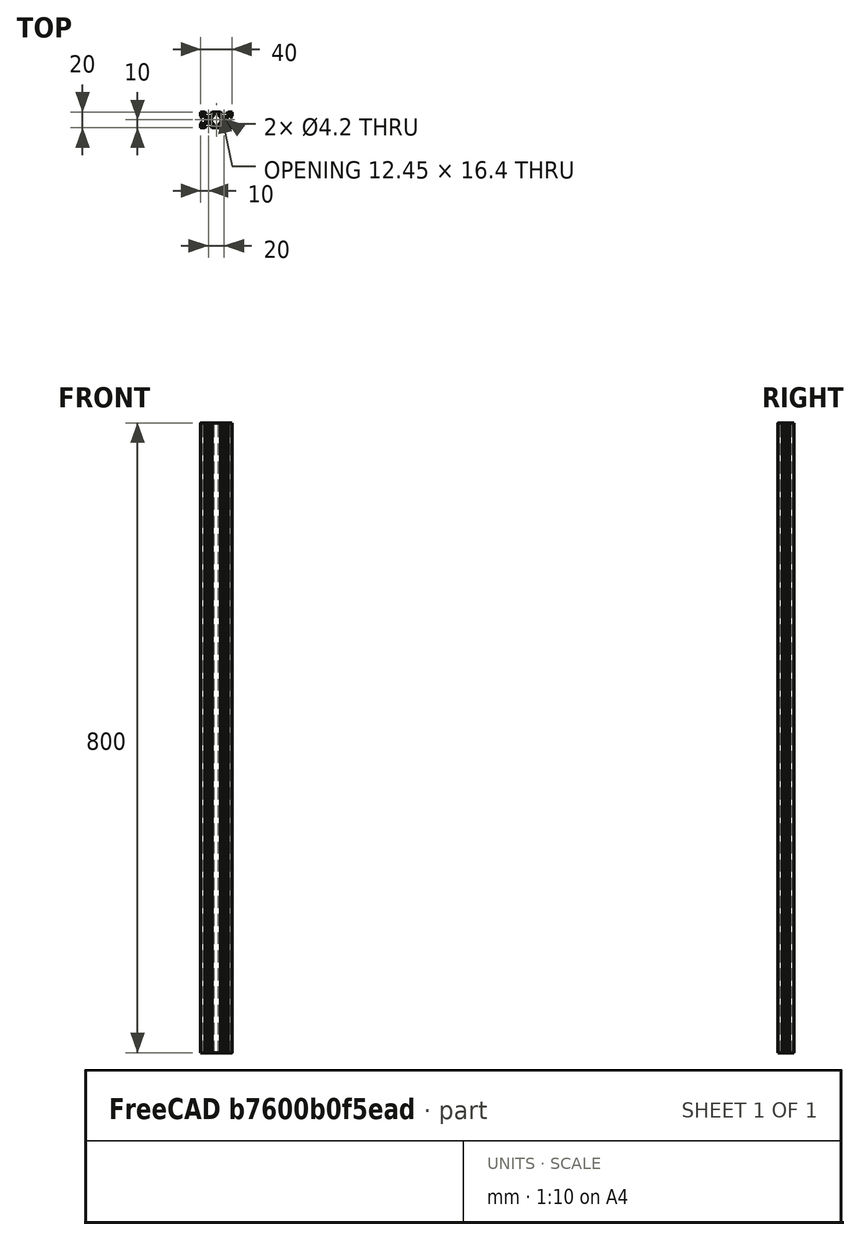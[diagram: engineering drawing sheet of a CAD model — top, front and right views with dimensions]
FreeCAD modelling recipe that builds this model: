
FCSTD DOCUMENT  (FreeCAD 0.20R25566 (Git))
Label: 2040-800
License: All rights reserved
LicenseURL: http://en.wikipedia.org/wiki/All_rights_reserved
objects: Sketcher::SketchObject×1, PartDesign::Pad×1, PartDesign::Body×1
note: 4 computed .brp shape members not serialized (recipe doc carries the construction recipe); baked Part::Feature solids carry a one-line shape summary decoded from their .brp

FEATURE [Sketcher::SketchObject] Sketch
  FullyConstrained = true
  MapMode = 5
  Support = -> [XY_Plane]
  sketch-geometry (114):
    g0: LineSegment StartX=-10 StartY=4.58 StartZ=0 EndX=-10 EndY=9.5 EndZ=0
    g1: LineSegment StartX=-9.5 StartY=10 StartZ=0 EndX=-4.58 EndY=10 EndZ=0
    g2: LineSegment StartX=-5.5 StartY=8.2 StartZ=0 EndX=-3.125 EndY=8.2 EndZ=0
    g3: LineSegment StartX=-8.2 StartY=5.5 StartZ=0 EndX=-8.2 EndY=3.125 EndZ=0
    g4: LineSegment StartX=-0.125 StartY=3.9 StartZ=0 EndX=-2.83934 EndY=3.9 EndZ=0
    g5: LineSegment StartX=-3.9 StartY=2.83934 StartZ=0 EndX=-3.9 EndY=0.125 EndZ=0
    g6: ArcOfCircle CenterX=0 CenterY=3.9 CenterZ=0 NormalX=0 NormalY=0 NormalZ=1 AngleXU=0 Radius=0.125 StartAngle=3.14159 EndAngle=6.28319
    g7: ArcOfCircle CenterX=-3.9 CenterY=0 CenterZ=0 NormalX=0 NormalY=0 NormalZ=1 AngleXU=0 Radius=0.125 StartAngle=4.71239 EndAngle=7.85398
    g8: ArcOfCircle CenterX=-9.5 CenterY=9.5 CenterZ=0 NormalX=0 NormalY=0 NormalZ=1 AngleXU=0 Radius=0.5 StartAngle=1.5708 EndAngle=3.14159
    g9: LineSegment StartX=-5.5 StartY=8.2 StartZ=0 EndX=-5.5 EndY=6.56066 EndZ=0
    g10: LineSegment StartX=-8.2 StartY=5.5 StartZ=0 EndX=-6.56066 EndY=5.5 EndZ=0
    g11: LineSegment StartX=-4.58 StartY=10 StartZ=0 EndX=-3.125 EndY=8.545 EndZ=0
    g12: LineSegment StartX=-3.125 StartY=8.545 StartZ=0 EndX=-3.125 EndY=8.2 EndZ=0
    g13: LineSegment StartX=-10 StartY=4.58 StartZ=0 EndX=-8.545 EndY=3.125 EndZ=0
    g14: LineSegment StartX=-8.545 StartY=3.125 StartZ=0 EndX=-8.2 EndY=3.125 EndZ=0
    g15: LineSegment StartX=-5.5 StartY=6.56066 StartZ=0 EndX=-2.83934 EndY=3.9 EndZ=0
    g16: LineSegment StartX=-6.56066 StartY=5.5 StartZ=0 EndX=-3.9 EndY=2.83934 EndZ=0
    g17: Circle CenterX=0 CenterY=0 CenterZ=0 NormalX=0 NormalY=0 NormalZ=1 AngleXU=0 Radius=2.1
    g18: LineSegment StartX=0.125 StartY=3.9 StartZ=0 EndX=2.83934 EndY=3.9 EndZ=0
    g19: LineSegment StartX=2.83934 StartY=3.9 StartZ=0 EndX=5.5 EndY=6.56066 EndZ=0
    g20: LineSegment StartX=5.5 StartY=6.56066 StartZ=0 EndX=5.5 EndY=8.2 EndZ=0
    g21: LineSegment StartX=3.125 StartY=8.2 StartZ=0 EndX=3.125 EndY=8.545 EndZ=0
    g22: LineSegment StartX=5.5 StartY=8.2 StartZ=0 EndX=3.125 EndY=8.2 EndZ=0
    g23: LineSegment StartX=7 StartY=5.93934 StartZ=0 EndX=3.9 EndY=2.83934 EndZ=0
    g24: LineSegment StartX=3.9 StartY=2.83934 StartZ=0 EndX=3.9 EndY=0.125 EndZ=0
    g25: ArcOfCircle CenterX=3.9 CenterY=0 CenterZ=0 NormalX=0 NormalY=0 NormalZ=1 AngleXU=0 Radius=0.125 StartAngle=1.5708 EndAngle=4.71239
    g26: LineSegment StartX=3.9 StartY=-0.125 StartZ=0 EndX=3.9 EndY=-2.83934 EndZ=0
    g27: LineSegment StartX=3.9 StartY=-2.83934 StartZ=0 EndX=7 EndY=-5.93934 EndZ=0
    g28: LineSegment StartX=4.58 StartY=-10 StartZ=0 EndX=3.125 EndY=-8.545 EndZ=0
    g29: LineSegment StartX=2.83934 StartY=-3.9 StartZ=0 EndX=5.5 EndY=-6.56066 EndZ=0
    g30: LineSegment StartX=3.125 StartY=-8.545 StartZ=0 EndX=3.125 EndY=-8.2 EndZ=0
    g31: LineSegment StartX=3.125 StartY=-8.2 StartZ=0 EndX=5.5 EndY=-8.2 EndZ=0
    g32: LineSegment StartX=5.5 StartY=-8.2 StartZ=0 EndX=5.5 EndY=-6.56066 EndZ=0
    g33: ArcOfCircle CenterX=0 CenterY=-3.9 CenterZ=0 NormalX=0 NormalY=0 NormalZ=1 AngleXU=0 Radius=0.125 StartAngle=0 EndAngle=3.14159
    g34: LineSegment StartX=0.125 StartY=-3.9 StartZ=0 EndX=2.83934 EndY=-3.9 EndZ=0
    g35: LineSegment StartX=-0.125 StartY=-3.9 StartZ=0 EndX=-2.83934 EndY=-3.9 EndZ=0
    g36: LineSegment StartX=-3.9 StartY=-0.125 StartZ=0 EndX=-3.9 EndY=-2.83934 EndZ=0
    g37: LineSegment StartX=-3.9 StartY=-2.83934 StartZ=0 EndX=-6.56066 EndY=-5.5 EndZ=0
    g38: LineSegment StartX=-6.56066 StartY=-5.5 StartZ=0 EndX=-8.2 EndY=-5.5 EndZ=0
    g39: LineSegment StartX=-8.2 StartY=-5.5 StartZ=0 EndX=-8.2 EndY=-3.125 EndZ=0
    g40: LineSegment StartX=-8.2 StartY=-3.125 StartZ=0 EndX=-8.545 EndY=-3.125 EndZ=0
    g41: LineSegment StartX=-8.545 StartY=-3.125 StartZ=0 EndX=-10 EndY=-4.58 EndZ=0
    g42: LineSegment StartX=-10 StartY=-4.58 StartZ=0 EndX=-10 EndY=-9.5 EndZ=0
    g43: ArcOfCircle CenterX=-9.5 CenterY=-9.5 CenterZ=0 NormalX=0 NormalY=0 NormalZ=1 AngleXU=0 Radius=0.5 StartAngle=3.14159 EndAngle=4.71239
    g44: LineSegment StartX=-9.5 StartY=-10 StartZ=0 EndX=-4.58 EndY=-10 EndZ=0
    g45: LineSegment StartX=-4.58 StartY=-10 StartZ=0 EndX=-3.125 EndY=-8.545 EndZ=0
    g46: LineSegment StartX=-2.83934 StartY=-3.9 StartZ=0 EndX=-5.5 EndY=-6.56066 EndZ=0
    g47: LineSegment StartX=-5.5 StartY=-6.56066 StartZ=0 EndX=-5.5 EndY=-8.2 EndZ=0
    g48: LineSegment StartX=-5.5 StartY=-8.2 StartZ=0 EndX=-3.125 EndY=-8.2 EndZ=0
    g49: LineSegment StartX=-3.125 StartY=-8.545 StartZ=0 EndX=-3.125 EndY=-8.2 EndZ=0
    g50: LineSegment StartX=3.125 StartY=8.545 StartZ=0 EndX=4.58 EndY=10 EndZ=0
    g51: LineSegment StartX=-3.9 StartY=2.83934 StartZ=0 EndX=-2.83934 EndY=3.9 EndZ=0
    g52: LineSegment StartX=3.9 StartY=2.83934 StartZ=0 EndX=2.83934 EndY=3.9 EndZ=0
    g53: LineSegment StartX=4.58 StartY=10 StartZ=0 EndX=15.42 EndY=10 EndZ=0
    g54: LineSegment StartX=4.58 StartY=-10 StartZ=0 EndX=15.42 EndY=-10 EndZ=0
    g55: LineSegment StartX=7 StartY=5.93934 StartZ=0 EndX=7 EndY=8.2 EndZ=0
    g56: LineSegment StartX=5.5 StartY=8.2 StartZ=0 EndX=7 EndY=8.2 EndZ=0
    g57: LineSegment StartX=7 StartY=-5.93934 StartZ=0 EndX=7 EndY=-8.2 EndZ=0
    g58: LineSegment StartX=7 StartY=8.2 StartZ=0 EndX=13 EndY=8.2 EndZ=0
    g59: LineSegment StartX=15.42 StartY=10 StartZ=0 EndX=16.875 EndY=8.545 EndZ=0
    g60: LineSegment StartX=16.875 StartY=8.545 StartZ=0 EndX=16.875 EndY=8.2 EndZ=0
    g61: LineSegment StartX=16.875 StartY=8.2 StartZ=0 EndX=14.5 EndY=8.2 EndZ=0
    g62: LineSegment StartX=15.42 StartY=-10 StartZ=0 EndX=16.875 EndY=-8.545 EndZ=0
    g63: LineSegment StartX=16.875 StartY=-8.545 StartZ=0 EndX=16.875 EndY=-8.2 EndZ=0
    g64: LineSegment StartX=16.875 StartY=-8.2 StartZ=0 EndX=14.5 EndY=-8.2 EndZ=0
    g65: LineSegment StartX=7 StartY=-8.2 StartZ=0 EndX=13 EndY=-8.2 EndZ=0
    g66: LineSegment StartX=13 StartY=8.2 StartZ=0 EndX=14.5 EndY=8.2 EndZ=0
    g67: LineSegment StartX=13 StartY=8.2 StartZ=0 EndX=13 EndY=5.93934 EndZ=0
    g68: LineSegment StartX=13 StartY=-8.2 StartZ=0 EndX=13 EndY=-5.93934 EndZ=0
    g69: LineSegment StartX=14.5 StartY=8.2 StartZ=0 EndX=14.5 EndY=6.56066 EndZ=0
    g70: LineSegment StartX=14.5 StartY=-8.2 StartZ=0 EndX=14.5 EndY=-6.56066 EndZ=0
    g71: LineSegment StartX=13 StartY=5.93934 StartZ=0 EndX=16.1 EndY=2.83934 EndZ=0
    g72: LineSegment StartX=14.5 StartY=6.56066 StartZ=0 EndX=17.1607 EndY=3.9 EndZ=0
    g73: LineSegment StartX=13 StartY=-5.93934 StartZ=0 EndX=16.1 EndY=-2.83934 EndZ=0
    g74: LineSegment StartX=14.5 StartY=-6.56066 StartZ=0 EndX=17.1607 EndY=-3.9 EndZ=0
    g75: LineSegment StartX=16.1 StartY=2.83934 StartZ=0 EndX=16.1 EndY=0.125 EndZ=0
    g76: LineSegment StartX=16.1 StartY=-2.83934 StartZ=0 EndX=16.1 EndY=-0.125 EndZ=0
    g77: ArcOfCircle CenterX=16.1 CenterY=0 CenterZ=0 NormalX=0 NormalY=0 NormalZ=1 AngleXU=0 Radius=0.125 StartAngle=4.71239 EndAngle=7.85398
    g78: LineSegment StartX=17.1607 StartY=3.9 StartZ=0 EndX=19.875 EndY=3.9 EndZ=0
    g79: LineSegment StartX=17.1607 StartY=-3.9 StartZ=0 EndX=19.875 EndY=-3.9 EndZ=0
    g80: LineSegment StartX=20.125 StartY=3.9 StartZ=0 EndX=22.8393 EndY=3.9 EndZ=0
    g81: LineSegment StartX=20.125 StartY=-3.9 StartZ=0 EndX=22.8393 EndY=-3.9 EndZ=0
    g82: ArcOfCircle CenterX=20 CenterY=-3.9 CenterZ=0 NormalX=0 NormalY=0 NormalZ=1 AngleXU=0 Radius=0.125 StartAngle=-9e-16 EndAngle=3.14159
    g83: ArcOfCircle CenterX=20 CenterY=3.9 CenterZ=0 NormalX=0 NormalY=0 NormalZ=1 AngleXU=0 Radius=0.125 StartAngle=3.14159 EndAngle=6.28319
    g84: Circle CenterX=20 CenterY=0 CenterZ=0 NormalX=0 NormalY=0 NormalZ=1 AngleXU=0 Radius=2.1
    g85: LineSegment StartX=22.8393 StartY=3.9 StartZ=0 EndX=25.5 EndY=6.56066 EndZ=0
    g86: LineSegment StartX=22.8393 StartY=-3.9 StartZ=0 EndX=25.5 EndY=-6.56066 EndZ=0
    g87: LineSegment StartX=25.5 StartY=6.56066 StartZ=0 EndX=25.5 EndY=8.2 EndZ=0
    g88: LineSegment StartX=25.5 StartY=-6.56066 StartZ=0 EndX=25.5 EndY=-8.2 EndZ=0
    g89: LineSegment StartX=25.5 StartY=8.2 StartZ=0 EndX=23.125 EndY=8.2 EndZ=0
    g90: LineSegment StartX=25.5 StartY=-8.2 StartZ=0 EndX=23.125 EndY=-8.2 EndZ=0
    g91: LineSegment StartX=23.125 StartY=8.2 StartZ=0 EndX=23.125 EndY=8.545 EndZ=0
    g92: LineSegment StartX=23.125 StartY=-8.2 StartZ=0 EndX=23.125 EndY=-8.545 EndZ=0
    g93: LineSegment StartX=23.125 StartY=8.545 StartZ=0 EndX=24.58 EndY=10 EndZ=0
    g94: LineSegment StartX=23.125 StartY=-8.545 StartZ=0 EndX=24.58 EndY=-10 EndZ=0
    g95: LineSegment StartX=24.58 StartY=10 StartZ=0 EndX=29.5 EndY=10 EndZ=0
    g96: LineSegment StartX=24.58 StartY=-10 StartZ=0 EndX=29.5 EndY=-10 EndZ=0
    g97: ArcOfCircle CenterX=29.5 CenterY=9.5 CenterZ=0 NormalX=0 NormalY=0 NormalZ=1 AngleXU=0 Radius=0.5 StartAngle=9e-16 EndAngle=1.5708
    g98: ArcOfCircle CenterX=29.5 CenterY=-9.5 CenterZ=0 NormalX=0 NormalY=0 NormalZ=1 AngleXU=0 Radius=0.5 StartAngle=4.71239 EndAngle=6.28319
    g99: LineSegment StartX=30 StartY=9.5 StartZ=0 EndX=30 EndY=4.58 EndZ=0
    g100: LineSegment StartX=30 StartY=-9.5 StartZ=0 EndX=30 EndY=-4.58 EndZ=0
    g101: LineSegment StartX=30 StartY=-4.58 StartZ=0 EndX=28.545 EndY=-3.125 EndZ=0
    g102: LineSegment StartX=30 StartY=4.58 StartZ=0 EndX=28.545 EndY=3.125 EndZ=0
    g103: LineSegment StartX=28.545 StartY=3.125 StartZ=0 EndX=28.2 EndY=3.125 EndZ=0
    g104: LineSegment StartX=28.545 StartY=-3.125 StartZ=0 EndX=28.2 EndY=-3.125 EndZ=0
    g105: LineSegment StartX=28.2 StartY=3.125 StartZ=0 EndX=28.2 EndY=5.5 EndZ=0
    g106: LineSegment StartX=28.2 StartY=-3.125 StartZ=0 EndX=28.2 EndY=-5.5 EndZ=0
    g107: LineSegment StartX=28.2 StartY=5.5 StartZ=0 EndX=26.5607 EndY=5.5 EndZ=0
    g108: LineSegment StartX=28.2 StartY=-5.5 StartZ=0 EndX=26.5607 EndY=-5.5 EndZ=0
    g109: LineSegment StartX=26.5607 StartY=5.5 StartZ=0 EndX=23.9 EndY=2.83934 EndZ=0
    g110: LineSegment StartX=26.5607 StartY=-5.5 StartZ=0 EndX=23.9 EndY=-2.83934 EndZ=0
    g111: LineSegment StartX=23.9 StartY=2.83934 StartZ=0 EndX=23.9 EndY=0.125 EndZ=0
    g112: LineSegment StartX=23.9 StartY=-2.83934 StartZ=0 EndX=23.9 EndY=-0.125 EndZ=0
    g113: ArcOfCircle CenterX=23.9 CenterY=3.14e-14 CenterZ=0 NormalX=0 NormalY=0 NormalZ=1 AngleXU=0 Radius=0.125 StartAngle=1.5708 EndAngle=4.71236
  constraints (345):
    c: Diameter(g17) = 4.2
    c: Radius(g25) = 0.125
    c: Coincident(g-1,g17)
    c: DistanceY(g43,g1) = 20
    c: Radius(g43) = 0.5
    c: DistanceX(g42,g17) = 10
    c: DistanceY(g43,g17) = 10
    c: Distance(g5,g4) = 1.5
    c: DistanceY(g18,g20) = 4.3
    c: DistanceX(g11,g21) = 6.25
    c: DistanceX(g1,g50) = 9.16
    c: DistanceX(g2,g20) = 11
    c: Coincident(g6,g18)
    c: Coincident(g6,g4)
    c: Coincident(g4,g15)
    c: Coincident(g18,g19)
    c: Coincident(g5,g16)
    c: Coincident(g16,g10)
    c: Coincident(g15,g9)
    c: Coincident(g12,g2)
    c: Coincident(g2,g9)
    c: Coincident(g12,g11)
    c: Coincident(g1,g11)
    c: Coincident(g22,g21)
    c: Coincident(g50,g21)
    c: Coincident(g22,g20)
    c: Coincident(g19,g20)
    c: Coincident(g0,g13)
    c: Coincident(g14,g13)
    c: Coincident(g14,g3)
    c: Coincident(g3,g10)
    c: Coincident(g5,g7)
    c: Coincident(g36,g7)
    c: Coincident(g37,g36)
    c: Coincident(g38,g37)
    c: Coincident(g38,g39)
    c: Coincident(g40,g39)
    c: Coincident(g41,g40)
    c: Coincident(g42,g41)
    c: Coincident(g44,g45)
    c: Coincident(g49,g45)
    c: Coincident(g48,g49)
    c: Coincident(g48,g47)
    c: Coincident(g46,g47)
    c: Coincident(g35,g46)
    c: Coincident(g33,g35)
    c: Coincident(g34,g33)
    c: Coincident(g34,g29)
    c: Coincident(g32,g29)
    c: Coincident(g31,g32)
    c: Coincident(g31,g30)
    c: Coincident(g28,g30)
    c: Coincident(g27,g26)
    c: Coincident(g24,g23)
    c: Coincident(g26,g25)
    c: Coincident(g25,g24)
    c: Vertical(g0)
    c: Horizontal(g1)
    c: Equal(g0,g1)
    c: Horizontal(g4)
    c: PointOnObject(g6,g-2)
    c: Horizontal(g18)
    c: Horizontal(g4,g6)
    c: Horizontal(g6,g6)
    c: Parallel(g13,g11)
    c: Horizontal(g14)
    c: Vertical(g12)
    c: Equal(g14,g12)
    c: Vertical(g3)
    c: Horizontal(g2)
    c: Equal(g3,g2)
    c: Equal(g10,g9)
    c: Horizontal(g10)
    c: Vertical(g9)
    c: Parallel(g16,g15)
    c: Equal(g13,g11)
    c: Tangent(g8,g0) = 1.5708
    c: PointOnObject(g7,g-1)
    c: Vertical(g5)
    c: Vertical(g36)
    c: Vertical(g7,g7)
    c: Vertical(g7,g5)
    c: Horizontal(g38)
    c: Vertical(g39)
    c: Horizontal(g40)
    c: Vertical(g42)
    c: Equal(g36,g5)
    c: Equal(g37,g16)
    c: Perpendicular(g16,g37)
    c: Equal(g38,g10)
    c: Equal(g39,g3)
    c: Equal(g40,g14)
    c: Equal(g41,g13)
    c: Perpendicular(g41,g13)
    c: Equal(g42,g0)
    c: Tangent(g43,g42) = -1.5708
    c: Tangent(g43,g44) = -1.5708
    c: Tangent(g8,g1) = 1.5708
    c: Equal(g43,g8)
    c: Horizontal(g44)
    c: Equal(g44,g42)
    c: Equal(g41,g45)
    c: Parallel(g41,g45)
    c: Vertical(g49)
    c: Equal(g49,g40)
    c: Horizontal(g48)
    c: Vertical(g47)
    c: Equal(g47,g38)
    c: Equal(g46,g37)
    c: Parallel(g46,g37)
    c: PointOnObject(g33,g-2)
    c: Horizontal(g33,g33)
    c: Horizontal(g33,g33)
    c: Horizontal(g35)
    c: Equal(g35,g36)
    c: Horizontal(g34)
    c: Vertical(g32)
    c: Perpendicular(g46,g29)
    c: Equal(g29,g46)
    c: Equal(g32,g47)
    c: Horizontal(g31)
    c: Equal(g31,g48)
    c: Vertical(g30)
    c: Equal(g30,g49)
    c: Perpendicular(g28,g45)
    c: Equal(g28,g45)
    c: Parallel(g29,g27)
    c: PointOnObject(g25,g-1)
    c: Vertical(g26)
    c: Vertical(g25,g24)
    c: Vertical(g24,g25)
    c: Equal(g34,g26)
    c: Equal(g33,g7)
    c: Equal(g7,g6)
    c: Vertical(g24)
    c: Equal(g26,g24)
    c: Equal(g4,g5)
    c: Equal(g4,g18)
    c: Parallel(g23,g19)
    c: Vertical(g20)
    c: Horizontal(g22)
    c: Equal(g22,g2)
    c: Vertical(g21)
    c: Equal(g11,g50)
    c: Horizontal(g2,g21)
    c: Vertical(g10,g37)
    c: Angle(g50,g11) = 1.5708
    c: DistanceY(g2,g1) = 1.8
    c: Equal(g21,g12)
    c: Horizontal(g36,g26)
    c: Vertical(g29,g18)
    c: Coincident(g51,g5)
    c: Coincident(g51,g4)
    c: Coincident(g52,g23)
    c: Coincident(g52,g18)
    c: Equal(g52,g51)
    c: Equal(g15,g19)
    c: Equal(g20,g9)
    c: Horizontal(g53)
    c: Horizontal(g54)
    c: Coincident(g55,g23)
    c: Vertical(g55)
    c: Horizontal(g55,g20)
    c: Coincident(g56,g20)
    c: Coincident(g56,g55)
    c: Equal(g56,g52)
    c: Coincident(g57,g27)
    c: Horizontal(g31,g57)
    c: Vertical(g57)
    c: Vertical(g27,g23)
    c: Coincident(g58,g55)
    c: Horizontal(g58)
    c: Coincident(g59,g53)
    c: Coincident(g60,g59)
    c: Vertical(g60)
    c: Coincident(g61,g60)
    c: Horizontal(g61)
    c: Coincident(g62,g54)
    c: Coincident(g63,g62)
    c: Vertical(g63)
    c: Coincident(g64,g63)
    c: Horizontal(g64)
    c: Coincident(g65,g57)
    c: Horizontal(g65)
    c: Equal(g22,g61)
    c: Equal(g64,g31)
    c: Equal(g59,g50)
    c: Equal(g62,g28)
    c: Equal(g21,g60)
    c: Equal(g30,g63)
    c: Perpendicular(g59,g50)
    c: Perpendicular(g62,g28)
    c: Equal(g58,g65)
    c: Coincident(g66,g58)
    c: Coincident(g66,g61)
    c: Equal(g56,g66)
    c: Coincident(g67,g58)
    c: Vertical(g67)
    c: Coincident(g68,g65)
    c: Vertical(g68)
    c: Coincident(g69,g61)
    c: Vertical(g69)
    c: Coincident(g70,g64)
    c: Vertical(g70)
    c: Equal(g55,g67)
    c: Equal(g57,g68)
    c: Equal(g20,g69)
    c: Equal(g32,g70)
    c: Coincident(g71,g67)
    c: Coincident(g72,g69)
    c: Coincident(g73,g68)
    c: Coincident(g74,g70)
    c: Equal(g23,g71)
    c: Perpendicular(g71,g23)
    c: Equal(g27,g73)
    c: Perpendicular(g73,g27)
    c: Equal(g72,g19)
    c: Perpendicular(g19,g72)
    c: Equal(g74,g29)
    c: Perpendicular(g29,g74)
    c: Coincident(g75,g71)
    c: Vertical(g75)
    c: Coincident(g76,g73)
    c: Vertical(g76)
    c: Equal(g24,g75)
    c: PointOnObject(g77,g-1)
    c: Coincident(g77,g75)
    c: Coincident(g77,g76)
    c: Equal(g25,g77)
    c: Coincident(g78,g72)
    c: Horizontal(g78)
    c: Coincident(g79,g74)
    c: Horizontal(g79)
    c: Equal(g18,g78)
    c: Equal(g34,g79)
    c: Horizontal(g80)
    c: Horizontal(g81)
    c: Equal(g79,g81)
    c: Equal(g78,g80)
    c: Horizontal(g78,g80)
    c: Horizontal(g79,g81)
    c: Coincident(g82,g79)
    c: Coincident(g82,g81)
    c: Coincident(g83,g78)
    c: Coincident(g83,g80)
    c: Equal(g77,g83)
    c: Equal(g77,g82)
    c: Horizontal(g83,g78)
    c: Horizontal(g79,g82)
    c: PointOnObject(g84,g-1)
    c: Equal(g17,g84)
    c: DistanceX(g17,g84) = 20
    c: Vertical(g70,g69)
    c: Coincident(g53,g50)
    c: Coincident(g54,g28)
    c: Vertical(g83,g84)
    c: Coincident(g85,g80)
    c: Coincident(g86,g81)
    c: Equal(g85,g19)
    c: Equal(g86,g29)
    c: Parallel(g19,g85)
    c: Parallel(g86,g29)
    c: Coincident(g87,g85)
    c: Coincident(g88,g86)
    c: Vertical(g88)
    c: Vertical(g87)
    c: Equal(g20,g87)
    c: Equal(g32,g88)
    c: Coincident(g89,g87)
    c: Horizontal(g89)
    c: Coincident(g90,g88)
    c: Horizontal(g90)
    c: Equal(g22,g89)
    c: Equal(g31,g90)
    c: Coincident(g91,g89)
    c: Vertical(g91)
    c: Coincident(g92,g90)
    c: Vertical(g92)
    c: Equal(g21,g91)
    c: Equal(g92,g30)
    c: Coincident(g93,g91)
    c: Coincident(g94,g92)
    c: Coincident(g95,g93)
    c: Horizontal(g95)
    c: Coincident(g96,g94)
    c: Horizontal(g96)
    c: Equal(g50,g93)
    c: Perpendicular(g93,g59)
    c: Equal(g94,g28)
    c: Perpendicular(g94,g62)
    c: Equal(g1,g95)
    c: Equal(g44,g96)
    c: Coincident(g97,g95)
    c: Coincident(g98,g96)
    c: Equal(g8,g97)
    c: Horizontal(g8,g97)
    c: Horizontal(g97,g97)
    c: Horizontal(g98,g43)
    c: Equal(g98,g43)
    c: Horizontal(g98,g98)
    c: Coincident(g99,g97)
    c: Vertical(g99)
    c: Coincident(g100,g98)
    c: Vertical(g100)
    c: Equal(g0,g99)
    c: Equal(g42,g100)
    c: Coincident(g101,g100)
    c: Coincident(g102,g99)
    c: Equal(g101,g41)
    c: Perpendicular(g101,g41)
    c: Equal(g102,g13)
    c: Perpendicular(g13,g102)
    c: Coincident(g103,g102)
    c: Horizontal(g103)
    c: Coincident(g104,g101)
    c: Horizontal(g104)
    c: Equal(g103,g14)
    c: Equal(g104,g40)
    c: Coincident(g105,g103)
    c: Vertical(g105)
    c: Coincident(g106,g104)
    c: Vertical(g106)
    c: Equal(g3,g105)
    c: Equal(g106,g39)
    c: Coincident(g107,g105)
    c: Horizontal(g107)
    c: Coincident(g108,g106)
    c: Horizontal(g108)
    c: Equal(g38,g108)
    c: Equal(g10,g107)
    c: Coincident(g109,g107)
    c: Coincident(g110,g108)
    c: Equal(g110,g37)
    c: Perpendicular(g37,g110)
    c: Equal(g109,g16)
    c: Perpendicular(g16,g109)
    c: Coincident(g111,g109)
    c: Vertical(g111)
    c: Coincident(g112,g110)
    c: Vertical(g112)
    c: Equal(g76,g112)
    c: Equal(g75,g111)
    c: Coincident(g113,g111)
    c: Coincident(g113,g112)
    c: Vertical(g113,g111)
FEATURE [PartDesign::Pad] Pad
  Direction = (0,0,1)
  Length = 800
  Length2 = 100
  Profile = -> Sketch
  Type = 0
FEATURE [PartDesign::Body] Body  label="2020-800"
  Group = -> [Sketch,Pad]
  Origin = -> Origin
  Tip = -> Pad
